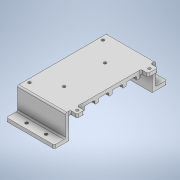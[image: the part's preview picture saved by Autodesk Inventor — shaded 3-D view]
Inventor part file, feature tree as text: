
AUTODESK INVENTOR PART (.ipt)
format: ipt  version: 2020 (Build 240168000, 168)  size: 331,776 bytes
history: native  units: in
note: dims shown in document units (in); Inventor stores cm internally (conversion verified against a paired STEP export)
features: extrude x5, sketch x5, fillet x4, hole x2, mirror x1, pattern_linear x1
ambient origin geometry x8: Origin, YZ Plane, XZ Plane, XY Plane, X Axis, Y Axis, Z Axis, Center Point
bodies: Solid1 (feature_tree)
feature tree (18):
  extrude  "Extrusion1"  Depth=4.7244in
  extrude  "Extrusion2"  Depth=6.378in
  extrude  "Extrusion3"  Depth=0.1969in TaperAngle=0.0deg
  hole  "Hole1"  [1 undecoded]
  mirror  "Mirror1"
  extrude  "Extrusion4"  Depth=0.0787in TaperAngle=0.0deg
  extrude  "Extrusion5"  Depth=0.0787in
  pattern_linear  "Rectangular Pattern1"  Spacing1=1.1024in  [1 undecoded]
  fillet  "Fillet1"  Radius=0.2953in
  fillet  "Fillet2"  Radius=0.2953in
  fillet  "Fillet3"  Radius=2.7244in
  fillet  "Fillet6"  Radius=4.5669in
  sketch  "Sketch1"  dims[d0=2.7244in d1=4.7244in]
  sketch  "Sketch3"  dims[d2=2.7244in d3=6.378in]
  sketch  "Sketch4"  dims[d4=0.7874in d5=0.1969in d6=0.0in]
  sketch  "Sketch5"  dims[d7=0.1969in d8=0.1969in]
  hole  "Hole Pattern"  [1 undecoded]
  sketch  "Sketch7"  dims[d9=1.2598in d10=0.0in d11=0.1969in d12=0.0in d13=0.7677in d14=1.1024in d15=0.2953in d16=0.2953in d17=0.1628in d18=0.3937in d19=0.1575in d20=0.0787in d21=90.0deg d22=0.5591in d23=0.8108in d24=2.7244in d25=4.5669in d26=0.1496in d27=0.1496in d29=0.1496in d30=0.1969in d31=2.5197in d32=0.9843in d33=1.3386in d34=3.3071in d35=1.3386in d36=4.3701in d37=2.5197in d38=0.1969in d39=0.0in d40=2.7244in d41=0.1969in d42=0.2165in d43=0.0in d44=1.1811in d46=0.7874in d47=1.1811in d49=0.7874in d50=0.0787in d51=0.0394in d52=0.0787in d53=0.3937in d54=0.4724in d55=0.3937in d56=0.6299in d59=0.3937in d60=0.3937in d61=0.3937in d62=0.5512in d63=0.0787in d71=0.2756in d72=0.1969in d73=0.1969in d74=0.1969in d75=0.1496in d76=0.1496in d77=0.1969in d78=0.1969in d79=0.2756in d80=0.1969in d81=0.1496in]
note: 3 required parameter values undecoded (feature->parameter linkage not recoverable at this tier; creation-order binding heuristic only, values carry confidence <= 0.55)
